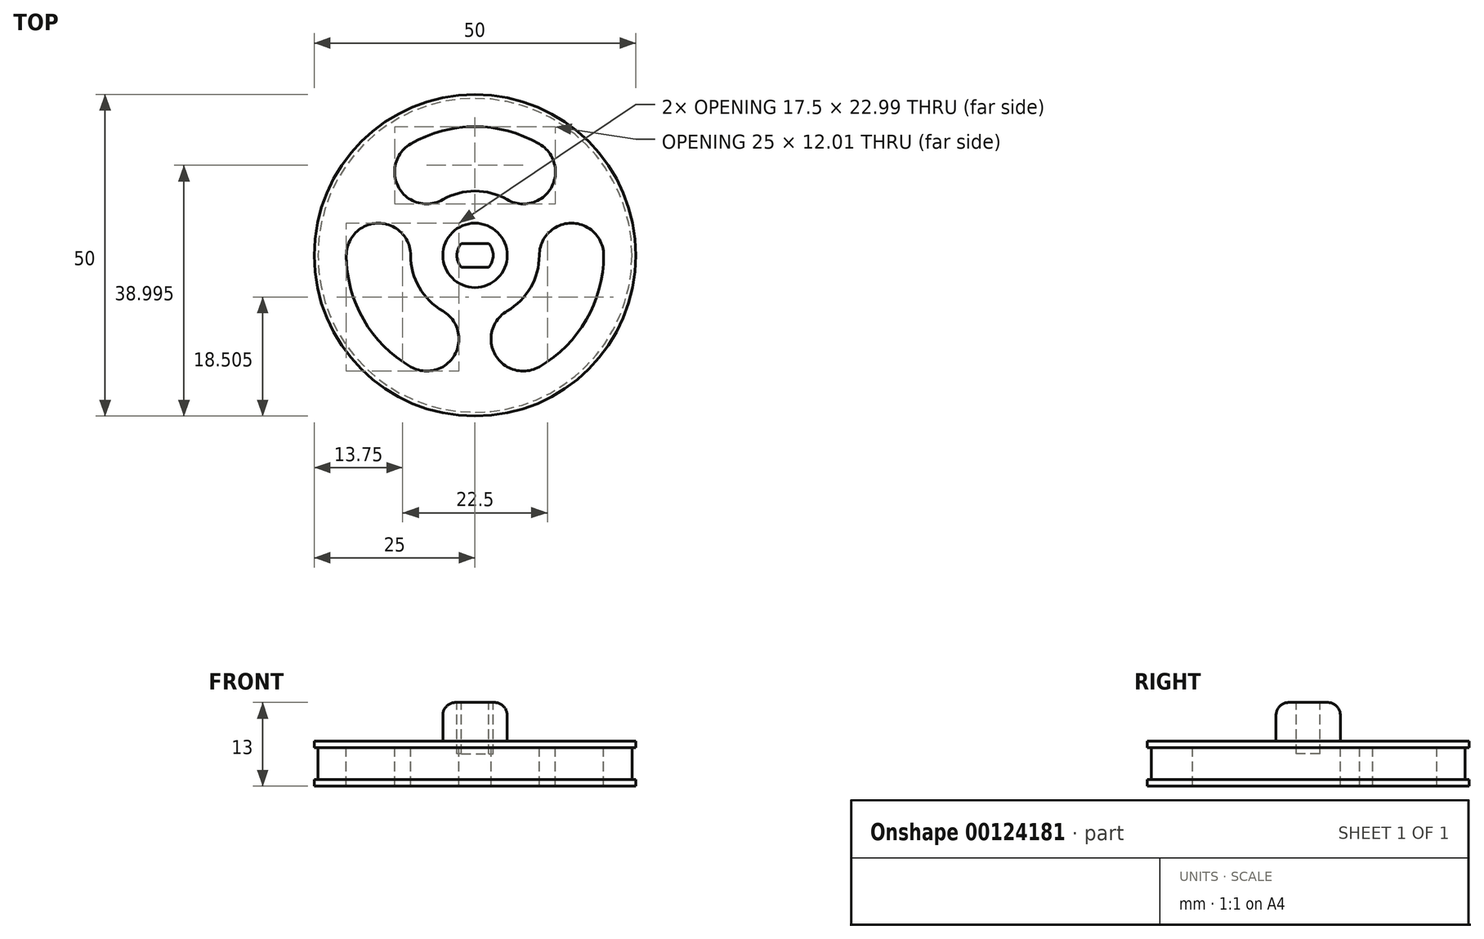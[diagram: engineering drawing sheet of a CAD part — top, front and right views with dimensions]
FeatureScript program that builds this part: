
annotation { "Feature Type Name" : "Feature", "Feature Type Description" : "" }
export const myFeature = defineFeature(function(context is Context, id is Id, definition is map)
    precondition{}
    {
        {
            var Q0;
            Q0=qCreatedBy(makeId("Top.planeOp"),FACE);
            var sketch = newSketch(context, id + "F0", { "sketchPlane" : qUnion([Q0])});
            skCircle(sketch, "E0", {"center": v(0, 0) * mm, "radius": 25 * mm});
            skSolve(sketch);
        }
        {
            var Q0;
            Q0=qSketchRegion(id+"F0",true);
            extrude(context, id + "F1", {"entities" : qUnion([Q0]), "depth" : 7 * mm});
        }
        {
            var Q0;
            Q0=makeQuery(id+"F1.opExtrude","CAP_FACE",FACE,{"disambiguationData":[OSD([sQuery(id+"F0.wireOp",EDGE,"E0")])],"isStart":false});
            var sketch = newSketch(context, id + "F2", { "sketchPlane" : qUnion([Q0])});
            skCircle(sketch, "E1", {"center": v(0, 0) * mm, "radius": 5 * mm});
            skSolve(sketch);
        }
        {
            var Q0;
            Q0=qSketchRegion(id+"F2",true);
            extrude(context, id + "F3", {"entities" : qUnion([Q0]), "operationType" : NewBodyOperationType.ADD, "depth" : 6 * mm});
        }
        {
            var Q0;
            Q0=makeQuery(id+"F3.opExtrude","CAP_FACE",FACE,{"disambiguationData":[OSD([sQuery(id+"F2.wireOp",EDGE,"E1")])],"isStart":false});
            var sketch = newSketch(context, id + "F4", { "sketchPlane" : qUnion([Q0])});
            skArc(sketch, "E2", {"start": v(-2.15, 1.82) * mm, "mid": v(-2.82, 0) * mm, "end": v(-2.15, -1.83) * mm});
            skLineSegment(sketch, "E3.bottom", {"start": v(-2.15, 1.83) * mm, "end": v(2.15, 1.83) * mm});
            skLineSegment(sketch, "E3.top", {"start": v(-2.15, -1.83) * mm, "end": v(2.15, -1.83) * mm});
            skArc(sketch, "E4.trimOffspring", {"start": v(2.15, -1.82) * mm, "mid": v(2.82, 0) * mm, "end": v(2.15, 1.83) * mm});
            skSolve(sketch);
        }
        {
            var Q0;
            Q0=qSketchRegion(id+"F4",true);
            extrude(context, id + "F5", {"entities" : qUnion([Q0]), "operationType" : NewBodyOperationType.REMOVE, "oppositeDirection" : true, "depth" : 8 * mm});
        }
        {
            var Q0;
            Q0=qCreatedBy(makeId("Top.planeOp"),FACE);
            cPlane(context, id + "F6", {"entities" : qUnion([Q0]), "cplaneType" : CPlaneType.OFFSET, "offset" : 1 * mm, "width" : 150 * mm, "height" : 150 * mm});
        }
        {
            var Q0;
            Q0=qCreatedBy(id+"F6.planeOp",FACE);
            var sketch = newSketch(context, id + "F7", { "sketchPlane" : qUnion([Q0])});
            skCircle(sketch, "E5.0", {"center": v(0, 0) * mm, "radius": 25 * mm});
            skCircle(sketch, "E6.0", {"center": v(0, 0) * mm, "radius": 24.4 * mm});
            skSolve(sketch);
        }
        {
            var Q0;
            Q0=qSketchRegion(id+"F7",true);
            extrude(context, id + "F8", {"entities" : qUnion([Q0]), "operationType" : NewBodyOperationType.REMOVE, "depth" : 5 * mm});
        }
        {
            var Q0;
            Q0=makeQuery(id+"F1.opExtrude","CAP_FACE",FACE,{"disambiguationData":[OSD([sQuery(id+"F0.wireOp",EDGE,"E0")])],"isStart":false});
            var sketch = newSketch(context, id + "F9", { "sketchPlane" : qUnion([Q0])});
            skCircle(sketch, "E7.0", {"center": v(0, 0) * mm, "radius": 20 * mm});
            skCircle(sketch, "E8.0", {"center": v(0, 0) * mm, "radius": 10 * mm});
            skLineSegment(sketch, "E9", {"start": v(0, -10) * mm, "end": v(0, -20) * mm, "construction": true});
            skLineSegment(sketch, "E10.bottom", {"start": v(-2.5, -9.68) * mm, "end": v(2.5, -9.68) * mm});
            skLineSegment(sketch, "E10.top", {"start": v(-2.5, -20.32) * mm, "end": v(2.5, -20.32) * mm});
            skLineSegment(sketch, "E10.left", {"start": v(-2.5, -9.68) * mm, "end": v(-2.5, -20.32) * mm});
            skLineSegment(sketch, "E10.right", {"start": v(2.5, -9.68) * mm, "end": v(2.5, -20.32) * mm});
            skPoint(sketch, "E10.middle", {"position": v(0, -15) * mm});
            skLineSegment(sketch, "E11.1.0", {"start": v(7.14, 7) * mm, "end": v(16.35, 12.32) * mm});
            skLineSegment(sketch, "E11.1.1", {"start": v(9.64, 2.68) * mm, "end": v(18.85, 8) * mm});
            skLineSegment(sketch, "E11.2.0", {"start": v(-9.64, 2.68) * mm, "end": v(-18.85, 8) * mm});
            skLineSegment(sketch, "E11.2.1", {"start": v(-7.14, 7) * mm, "end": v(-16.35, 12.32) * mm});
            skSolve(sketch);
        }
        {
            var Q0;
            {var subQ0=sQuery(id+"F9.wireOp",EDGE,"E11.1.0");var subQ1=sQuery(id+"F9.wireOp",EDGE,"E7.0");var subQ2=makeQuery(id+"F9.imprint","INTERSECT",VERTEX,{"derivedFrom":[subQ1,subQ0]});Q0=makeQuery(id+"F9.imprint","IMPRINT",FACE,{"disambiguationData":[TD([[makeQuery(id+"F9.imprint","IMPRINT",EDGE,{"disambiguationData":[TD([[subQ2,-1.0]])],"derivedFrom":subQ1}),1.0]])]});}
            var Q1;
            {var subQ0=sQuery(id+"F9.wireOp",EDGE,"E11.1.1");var subQ1=sQuery(id+"F9.wireOp",EDGE,"E7.0");var subQ2=makeQuery(id+"F9.imprint","INTERSECT",VERTEX,{"derivedFrom":[subQ1,subQ0]});Q1=makeQuery(id+"F9.imprint","IMPRINT",FACE,{"disambiguationData":[TD([[makeQuery(id+"F9.imprint","IMPRINT",EDGE,{"disambiguationData":[TD([[subQ2,1.0]])],"derivedFrom":subQ1}),1.0]])]});}
            var Q2;
            {var subQ0=sQuery(id+"F9.wireOp",EDGE,"E11.2.0");var subQ1=sQuery(id+"F9.wireOp",EDGE,"E7.0");var subQ2=makeQuery(id+"F9.imprint","INTERSECT",VERTEX,{"derivedFrom":[subQ1,subQ0]});Q2=makeQuery(id+"F9.imprint","IMPRINT",FACE,{"disambiguationData":[TD([[makeQuery(id+"F9.imprint","IMPRINT",EDGE,{"disambiguationData":[TD([[subQ2,-1.0]])],"derivedFrom":subQ1}),1.0]])]});}
            extrude(context, id + "F10", {"entities" : qUnion([Q0, Q1, Q2]), "operationType" : NewBodyOperationType.REMOVE, "oppositeDirection" : true, "depth" : 25 * mm});
        }
        {
            var Q0;
            Q0=makeQuery(id+"F10.boolean.opBoolean","COPY",EDGE,{"derivedFrom":makeQuery(id+"F10.opExtrude","SWEPT_EDGE",EDGE,{"disambiguationData":[OSD([sQuery(id+"F9.wireOp",EDGE,"E7.0"),sQuery(id+"F9.wireOp",EDGE,"E11.2.0")])]})});
            var Q1;
            Q1=makeQuery(id+"F10.boolean.opBoolean","COPY",EDGE,{"derivedFrom":makeQuery(id+"F10.opExtrude","SWEPT_EDGE",EDGE,{"disambiguationData":[OSD([sQuery(id+"F9.wireOp",EDGE,"E7.0"),sQuery(id+"F9.wireOp",EDGE,"E11.2.1")])]})});
            var Q2;
            Q2=makeQuery(id+"F10.boolean.opBoolean","COPY",EDGE,{"derivedFrom":makeQuery(id+"F10.opExtrude","SWEPT_EDGE",EDGE,{"disambiguationData":[OSD([sQuery(id+"F9.wireOp",EDGE,"E7.0"),sQuery(id+"F9.wireOp",EDGE,"E11.1.0")])]})});
            var Q3;
            Q3=makeQuery(id+"F10.boolean.opBoolean","COPY",EDGE,{"derivedFrom":makeQuery(id+"F10.opExtrude","SWEPT_EDGE",EDGE,{"disambiguationData":[OSD([sQuery(id+"F9.wireOp",EDGE,"E7.0"),sQuery(id+"F9.wireOp",EDGE,"E11.1.1")])]})});
            var Q4;
            Q4=makeQuery(id+"F10.boolean.opBoolean","COPY",EDGE,{"derivedFrom":makeQuery(id+"F10.opExtrude","SWEPT_EDGE",EDGE,{"disambiguationData":[OSD([sQuery(id+"F9.wireOp",EDGE,"E7.0"),sQuery(id+"F9.wireOp",EDGE,"E10.right")])]})});
            var Q5;
            Q5=makeQuery(id+"F10.boolean.opBoolean","COPY",EDGE,{"derivedFrom":makeQuery(id+"F10.opExtrude","SWEPT_EDGE",EDGE,{"disambiguationData":[OSD([sQuery(id+"F9.wireOp",EDGE,"E7.0"),sQuery(id+"F9.wireOp",EDGE,"E10.left")])]})});
            fillet(context, id + "F11", {"entities" : qUnion([Q0, Q1, Q2, Q3, Q4, Q5]), "radius" : 5 * mm, "tangentPropagation" : true, "allowEdgeOverflow" : false});
        }
        {
            var Q0;
            Q0=makeQuery(id+"F10.boolean.opBoolean","COPY",EDGE,{"derivedFrom":makeQuery(id+"F10.opExtrude","SWEPT_EDGE",EDGE,{"disambiguationData":[OSD([sQuery(id+"F9.wireOp",EDGE,"E8.0"),sQuery(id+"F9.wireOp",EDGE,"E11.2.0")])]})});
            var Q1;
            Q1=makeQuery(id+"F10.boolean.opBoolean","COPY",EDGE,{"derivedFrom":makeQuery(id+"F10.opExtrude","SWEPT_EDGE",EDGE,{"disambiguationData":[OSD([sQuery(id+"F9.wireOp",EDGE,"E8.0"),sQuery(id+"F9.wireOp",EDGE,"E10.bottom"),sQuery(id+"F9.wireOp",EDGE,"E10.left")])]})});
            var Q2;
            Q2=makeQuery(id+"F10.boolean.opBoolean","COPY",EDGE,{"derivedFrom":makeQuery(id+"F10.opExtrude","SWEPT_EDGE",EDGE,{"disambiguationData":[OSD([sQuery(id+"F9.wireOp",EDGE,"E8.0"),sQuery(id+"F9.wireOp",EDGE,"E10.bottom"),sQuery(id+"F9.wireOp",EDGE,"E10.right")])]})});
            var Q3;
            Q3=makeQuery(id+"F10.boolean.opBoolean","COPY",EDGE,{"derivedFrom":makeQuery(id+"F10.opExtrude","SWEPT_EDGE",EDGE,{"disambiguationData":[OSD([sQuery(id+"F9.wireOp",EDGE,"E8.0"),sQuery(id+"F9.wireOp",EDGE,"E11.1.1")])]})});
            var Q4;
            Q4=makeQuery(id+"F10.boolean.opBoolean","COPY",EDGE,{"derivedFrom":makeQuery(id+"F10.opExtrude","SWEPT_EDGE",EDGE,{"disambiguationData":[OSD([sQuery(id+"F9.wireOp",EDGE,"E8.0"),sQuery(id+"F9.wireOp",EDGE,"E11.1.0")])]})});
            var Q5;
            Q5=makeQuery(id+"F10.boolean.opBoolean","COPY",EDGE,{"derivedFrom":makeQuery(id+"F10.opExtrude","SWEPT_EDGE",EDGE,{"disambiguationData":[OSD([sQuery(id+"F9.wireOp",EDGE,"E8.0"),sQuery(id+"F9.wireOp",EDGE,"E11.2.1")])]})});
            fillet(context, id + "F12", {"entities" : qUnion([Q0, Q1, Q2, Q3, Q4, Q5]), "radius" : 5 * mm, "tangentPropagation" : true, "allowEdgeOverflow" : false});
        }
        {
            var Q0;
            Q0=makeQuery(id+"F3.opExtrude","CAP_EDGE",EDGE,{"disambiguationData":[OSD([sQuery(id+"F2.wireOp",EDGE,"E1")])],"isStart":true});
            var Q1;
            Q1=makeQuery(id+"F3.opExtrude","CAP_EDGE",EDGE,{"disambiguationData":[OSD([sQuery(id+"F2.wireOp",EDGE,"E1")])],"isStart":false});
            fillet(context, id + "F13", {"entities" : qUnion([Q0, Q1]), "radius" : 2 * mm, "tangentPropagation" : true, "allowEdgeOverflow" : false});
        }
    });
